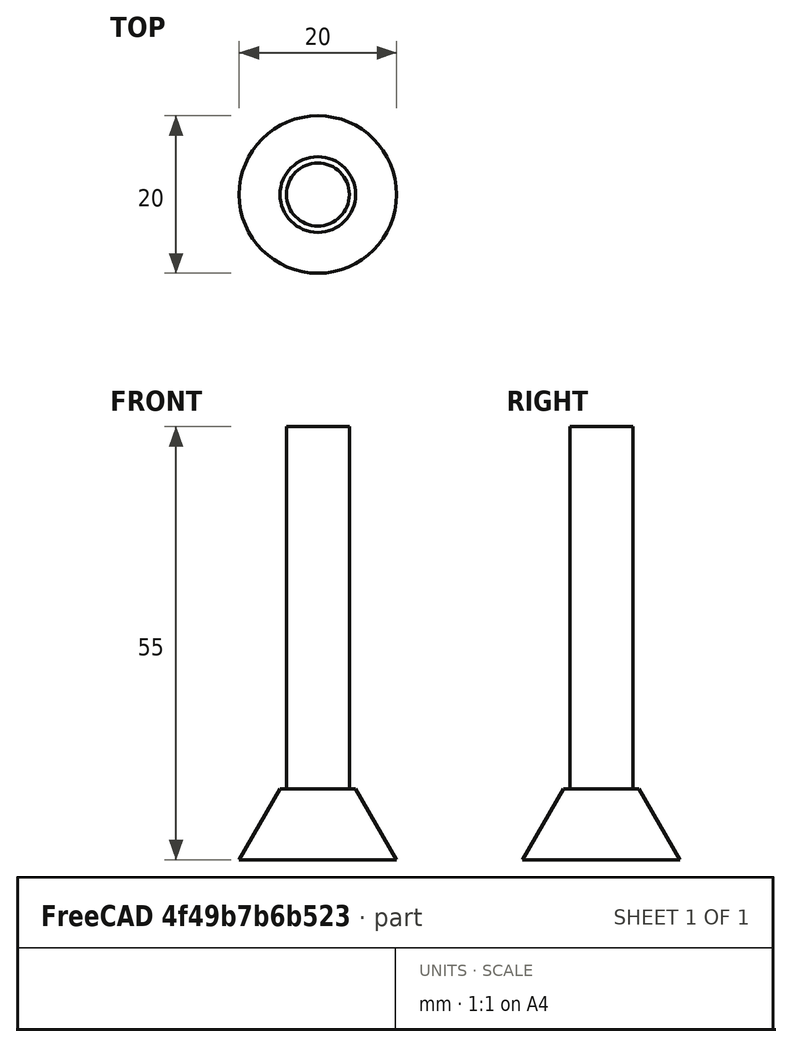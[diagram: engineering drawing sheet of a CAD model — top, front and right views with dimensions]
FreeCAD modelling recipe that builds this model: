
FCSTD DOCUMENT  (FreeCAD 1.0R39109 (Git))
Label: dovetail
License: Creative Commons Attribution 4.0
LicenseURL: https://creativecommons.org/licenses/by/4.0/
objects: Sketcher::SketchObject×1, PartDesign::Revolution×1, App::FeaturePython×1, PartDesign::Body×1
note: 6 computed .brp shape members not serialized (recipe doc carries the construction recipe); baked Part::Feature solids carry a one-line shape summary decoded from their .brp

FEATURE [Sketcher::SketchObject] Sketch
  ArcFitTolerance = 0
  AttachmentSupport = -> [XZ_Plane]
  FullyConstrained = true
  MakeInternals = false
  MapMode = 5
  Placement = pos=(0,0,0) rot=(1,0,0;1.5708rad)
  expr: Constraints[13] = <<Attributes>>.ShankDiameter
  expr: Constraints[14] = <<Attributes>>.CuttingEdgeHeight
  expr: Constraints[21] = <<Attributes>>.CuttingEdgeAngle
  expr: Constraints[28] = <<Attributes>>.NeckHeight
  expr: Constraints[31] = <<Attributes>>.NeckDiameter
  expr: Constraints[7] = <<Attributes>>.Diameter
  expr: Constraints[8] = <<Attributes>>.Length
  sketch-geometry (13):
    g0: LineSegment StartX=0 StartY=55 StartZ=0 EndX=0 EndY=0 EndZ=0
    g1: LineSegment StartX=0 StartY=0 StartZ=0 EndX=10 EndY=0 EndZ=0
    g2: LineSegment StartX=10 StartY=0 StartZ=0 EndX=4.80385 EndY=9 EndZ=0
    g3: LineSegment StartX=4 StartY=55 StartZ=0 EndX=0 EndY=55 EndZ=0
    g4: LineSegment [constr] StartX=10 StartY=0 StartZ=0 EndX=-10 EndY=0 EndZ=0
    g5: LineSegment StartX=4 StartY=55 StartZ=0 EndX=4 EndY=14 EndZ=0
    g6: LineSegment [constr] StartX=-4 StartY=55 StartZ=0 EndX=4 EndY=55 EndZ=0
    g7: LineSegment [constr] StartX=4.80385 StartY=9 StartZ=0 EndX=-4.80385 EndY=9 EndZ=0
    g8: LineSegment [constr] StartX=-10 StartY=0 StartZ=0 EndX=-4.80385 EndY=9 EndZ=0
    g9: LineSegment StartX=4.80385 StartY=9 StartZ=0 EndX=4 EndY=9 EndZ=0
    g10: LineSegment StartX=4 StartY=9 StartZ=0 EndX=4 EndY=14 EndZ=0
    g11: LineSegment StartX=4 StartY=14 StartZ=0 EndX=4 EndY=14 EndZ=0
    g12: GeomPoint [constr] X=-4 Y=9 Z=0
  constraints (32):
    c: Vertical(g0)
    c: Coincident(g0,g1)
    c: Horizontal(g1)
    c: Coincident(g1,g2)
    c: Horizontal(g3)
    c: Coincident(g4,g1)
    c: Symmetric(g1,g4,g0)
    c: DistanceX(g4,g4) = 20
    c: DistanceY(g2,g3) = 55
    c: Vertical(g5)
    c: Coincident(g3,g5)
    c: Symmetric(g6,g6,g0)
    c: Coincident(g6,g3)
    c: DistanceX(g6,g6) = 8
    c: DistanceY(g2) = 9
    c: Coincident(g0,g-1)
    c: Coincident(g0,g3)
    c: Coincident(g7,g2)
    c: Symmetric(g7,g2,g0)
    c: Coincident(g8,g4)
    c: Coincident(g8,g7)
    c: Angle(g2,g1) = 1.0472
    c: Coincident(g2,g9)
    c: PointOnObject(g9,g7)
    c: Coincident(g9,g10)
    c: Vertical(g10)
    c: Coincident(g10,g11)
    c: Horizontal(g11)
    c: DistanceY(g10,g10) = 5
    c: Coincident(g11,g5)
    c: Symmetric(g12,g9,g0)
    c: DistanceX(g12,g9) = 8
FEATURE [PartDesign::Revolution] Revolution
  AllowMultiFace = false
  Angle = 360
  Angle2 = 60
  Axis = (0,2e-16,1)
  Base = (0,0,0)
  Placement = pos=(0,0,0) rot=(1,0,0;1.5708rad)
  Profile = -> Sketch
  ReferenceAxis = -> Sketch [V_Axis]
  Reversed = true
  Suppressed = false
  Type = 0
FEATURE [App::FeaturePython] PropertyBag  label="Attributes"  # WARN: FeaturePython — macro-defined, semantics opaque (R4)
  CustomPropertyGroups = 0
  CuttingEdgeAngle = 60
  CuttingEdgeHeight = 9
  Diameter = 20
  Flutes = 8
  Length = 55
  NeckDiameter = 8
  NeckHeight = 5
  ShankDiameter = 8
  TipDiameter = 5
FEATURE [PartDesign::Body] Body  label="Dovetail"
  AllowCompound = false
  Group = -> [Sketch,Revolution,PropertyBag]
  Origin = -> Origin
  Tip = -> Revolution
